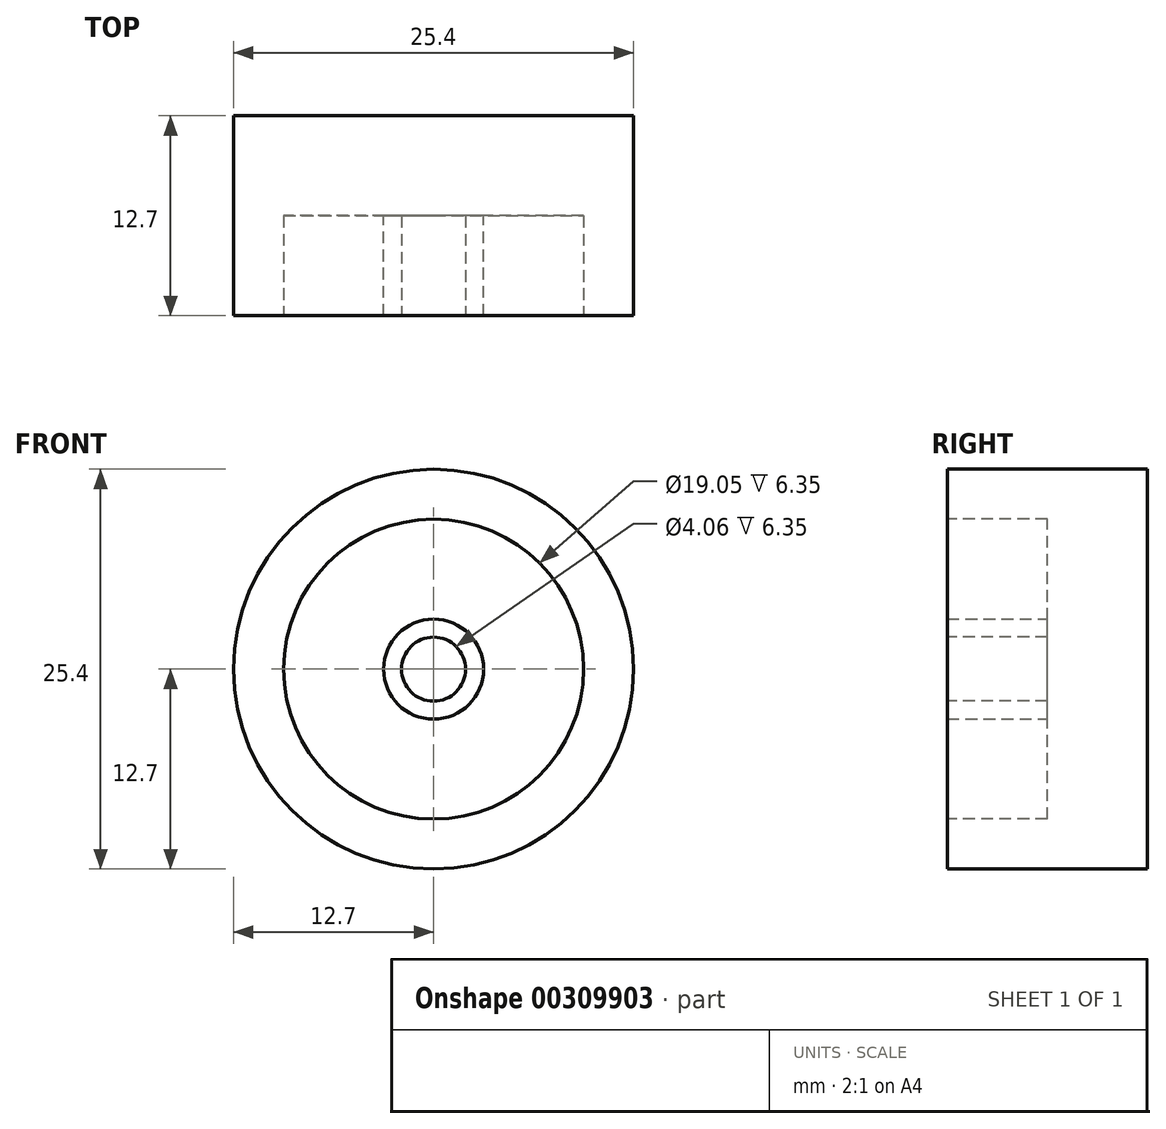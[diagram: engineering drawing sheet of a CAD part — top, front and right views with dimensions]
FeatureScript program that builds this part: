
annotation { "Feature Type Name" : "Feature", "Feature Type Description" : "" }
export const myFeature = defineFeature(function(context is Context, id is Id, definition is map)
    precondition{}
    {
        {
            var Q0;
            Q0=qCreatedBy(makeId("Front.planeOp"),FACE);
            var sketch = newSketch(context, id + "F0", { "sketchPlane" : qUnion([Q0])});
            skCircle(sketch, "E0", {"center": v(0, 0) * mm, "radius": 12.7 * mm});
            skSolve(sketch);
        }
        {
            var Q0;
            Q0=makeQuery(id+"F0.imprint","IMPRINT",FACE,{"disambiguationData":[TD([[makeQuery(id+"F0.imprint","IMPRINT",EDGE,{"derivedFrom":sQuery(id+"F0.wireOp",EDGE,"E0")}),1.0]])]});
            extrude(context, id + "F1", {"entities" : qUnion([Q0]), "depth" : 12.7 * mm});
        }
        {
            var Q0;
            Q0=makeQuery(id+"F1.opExtrude","CAP_FACE",FACE,{"disambiguationData":[OSD([sQuery(id+"F0.wireOp",EDGE,"E0")])],"isStart":false});
            var sketch = newSketch(context, id + "F2", { "sketchPlane" : qUnion([Q0])});
            skCircle(sketch, "E1", {"center": v(0, 0) * mm, "radius": 9.53 * mm});
            skSolve(sketch);
        }
        {
            var Q0;
            Q0 = qSketchRegion(id + "F2", true);
            extrude(context, id + "F3", {"entities" : qUnion([Q0]), "operationType" : NewBodyOperationType.REMOVE, "oppositeDirection" : true, "depth" : 6.35 * mm});
        }
        {
            var Q0;
            Q0=makeQuery(id+"F3.boolean.opBoolean","COPY",FACE,{"derivedFrom":makeQuery(id+"F3.opExtrude","CAP_FACE",FACE,{"disambiguationData":[OSD([sQuery(id+"F2.wireOp",EDGE,"E1")])],"isStart":false})});
            var sketch = newSketch(context, id + "F4", { "sketchPlane" : qUnion([Q0])});
            skCircle(sketch, "E2", {"center": v(0, 0) * mm, "radius": 3.18 * mm});
            skSolve(sketch);
        }
        {
            var Q0;
            Q0 = qSketchRegion(id + "F4", true);
            var Q1;
            Q1=makeQuery(id+"F1.opExtrude","CAP_FACE",FACE,{"disambiguationData":[OSD([sQuery(id+"F0.wireOp",EDGE,"E0")])],"isStart":false});
            extrude(context, id + "F5", {"entities" : qUnion([Q0]), "operationType" : NewBodyOperationType.ADD, "endBound" : BoundingType.UP_TO_SURFACE, "endBoundEntityFace" : qUnion([Q1]), "depth" : 25.4 * mm});
        }
        {
            var Q0;
            Q0=makeQuery(id+"F5.opExtrude","CAP_FACE",FACE,{"disambiguationData":[OSD([sQuery(id+"F4.wireOp",EDGE,"E2")])],"isStart":false});
            var sketch = newSketch(context, id + "F6", { "sketchPlane" : qUnion([Q0])});
            skCircle(sketch, "E3", {"center": v(0, 0) * mm, "radius": 2.03 * mm});
            skSolve(sketch);
        }
        {
            var Q0;
            Q0=makeQuery(id+"F6.imprint","IMPRINT",FACE,{"disambiguationData":[TD([[makeQuery(id+"F6.imprint","IMPRINT",EDGE,{"derivedFrom":sQuery(id+"F6.wireOp",EDGE,"E3")}),1.0]])]});
            var Q1;
            Q1=makeQuery(id+"F3.boolean.opBoolean","COPY",FACE,{"derivedFrom":makeQuery(id+"F3.opExtrude","CAP_FACE",FACE,{"disambiguationData":[OSD([sQuery(id+"F2.wireOp",EDGE,"E1")])],"isStart":false})});
            extrude(context, id + "F7", {"entities" : qUnion([Q0]), "operationType" : NewBodyOperationType.REMOVE, "endBound" : BoundingType.UP_TO_SURFACE, "oppositeDirection" : true, "endBoundEntityFace" : qUnion([Q1]), "depth" : 25.4 * mm});
        }
    });
